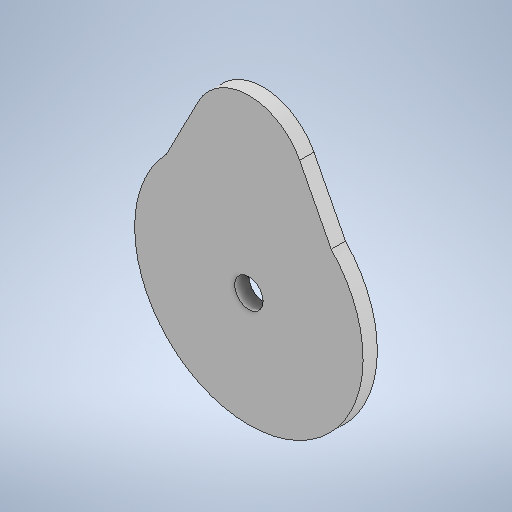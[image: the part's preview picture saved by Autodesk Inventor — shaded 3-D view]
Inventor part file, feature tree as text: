
AUTODESK INVENTOR PART (.ipt)
format: ipt  version: 2025 (Build 290162010, 162A)  size: 257,024 bytes
history: native  units: in
note: dims shown in document units (in); Inventor stores cm internally (conversion verified against a paired STEP export)
features: extrude x4, sketch x3, delete_face x3
ambient origin geometry x8: Origin, YZ Plane, XZ Plane, XY Plane, X Axis, Y Axis, Z Axis, Center Point
bodies: Solid1 (feature_tree)
feature tree (10):
  extrude  "Extrusion1"  Depth=1.0in
  extrude  "Extrusion2"  Depth=0.1875in TaperAngle=0.0deg
  sketch  "Sketch3"  dims[d2=1.0in d3=0.1875in d4=0.0in]
  delete_face  "Delete Face1"
  delete_face  "Delete Face2"
  delete_face  "Delete Face3"
  extrude  "Extrusion3"  Depth=0.1875in TaperAngle=0.0deg
  extrude  "Extrusion4"  Depth=0.125in TaperAngle=0.0deg
  sketch  "Sketch1"  dims[d0=2.0in d1=1.0in]
  sketch  "Sketch4"  dims[d5=0.25in d6=0.1875in d7=0.0in d8=0.125in d9=0.0in d10=0.25in d11=0.125in d12=0.0in]
